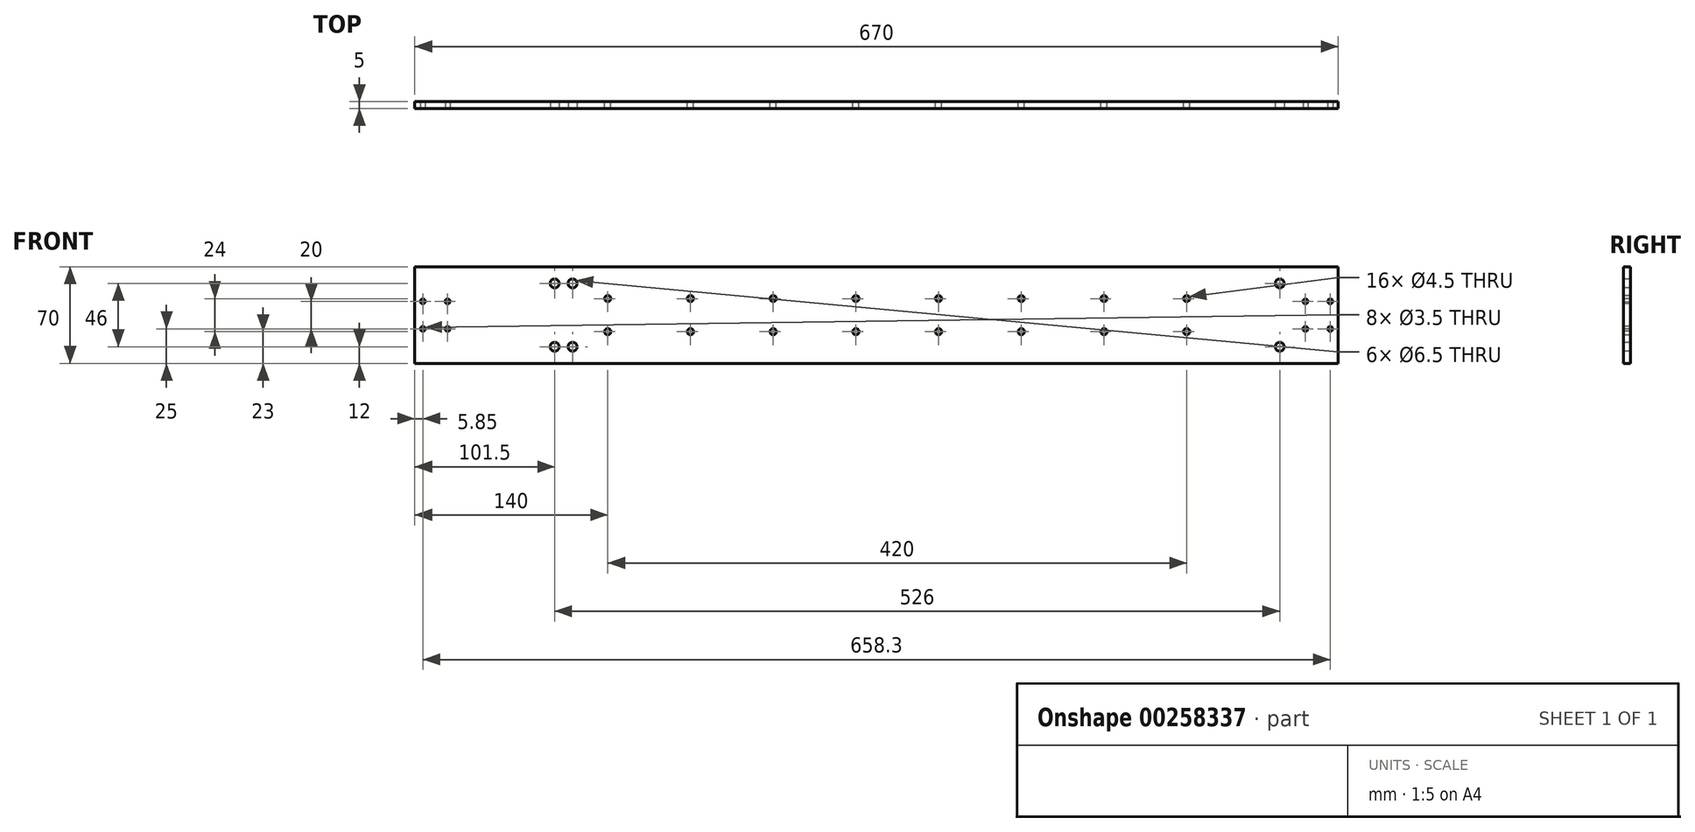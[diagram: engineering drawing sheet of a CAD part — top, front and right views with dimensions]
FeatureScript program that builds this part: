
annotation { "Feature Type Name" : "Feature", "Feature Type Description" : "" }
export const myFeature = defineFeature(function(context is Context, id is Id, definition is map)
    precondition{}
    {
        {
            var Q0;
            Q0=qCreatedBy(makeId("Front.planeOp"),FACE);
            var sketch = newSketch(context, id + "F0", { "sketchPlane" : qUnion([Q0])});
            skLineSegment(sketch, "E0.bottom", {"start": v(335, -35) * mm, "end": v(-335, -35) * mm});
            skLineSegment(sketch, "E0.top", {"start": v(335, 35) * mm, "end": v(-335, 35) * mm});
            skLineSegment(sketch, "E0.left", {"start": v(335, -35) * mm, "end": v(335, 35) * mm});
            skLineSegment(sketch, "E0.right", {"start": v(-335, -35) * mm, "end": v(-335, 35) * mm});
            skPoint(sketch, "E0.middle", {"position": v(0, 0) * mm});
            skSolve(sketch);
        }
        {
            var Q0;
            Q0 = qSketchRegion(id + "F0", true);
            extrude(context, id + "F1", {"entities" : qUnion([Q0]), "depth" : 5 * mm});
        }
        {
            var Q0;
            Q0=makeQuery(id+"F1.opExtrude","CAP_FACE",FACE,{"disambiguationData":[OSD([sQuery(id+"F0.wireOp",EDGE,"E0.bottom"),sQuery(id+"F0.wireOp",EDGE,"E0.top"),sQuery(id+"F0.wireOp",EDGE,"E0.left"),sQuery(id+"F0.wireOp",EDGE,"E0.right")])],"isStart":false});
            var sketch = newSketch(context, id + "F2", { "sketchPlane" : qUnion([Q0])});
            skLineSegment(sketch, "E1", {"start": v(-335, 0) * mm, "end": v(335, 0) * mm, "construction": true});
            skLineSegment(sketch, "E2", {"start": v(0, 35) * mm, "end": v(0, -35) * mm, "construction": true});
            skCircle(sketch, "E3", {"center": v(-329.15, 10) * mm, "radius": 1.75 * mm});
            skCircle(sketch, "E4", {"center": v(-311.15, 10) * mm, "radius": 1.75 * mm});
            skCircle(sketch, "E5", {"center": v(-329.15, -10) * mm, "radius": 1.75 * mm});
            skCircle(sketch, "E6", {"center": v(-311.15, -10) * mm, "radius": 1.75 * mm});
            skCircle(sketch, "E7.MirrorC", {"center": v(329.15, 10) * mm, "radius": 1.75 * mm});
            skCircle(sketch, "E8.MirrorC", {"center": v(311.15, 10) * mm, "radius": 1.75 * mm});
            skCircle(sketch, "E9.MirrorC", {"center": v(311.15, -10) * mm, "radius": 1.75 * mm});
            skCircle(sketch, "E10.MirrorC", {"center": v(329.15, -10) * mm, "radius": 1.75 * mm});
            skSolve(sketch);
        }
        {
            var Q0;
            Q0 = qSketchRegion(id + "F2", true);
            extrude(context, id + "F3", {"entities" : qUnion([Q0]), "operationType" : NewBodyOperationType.REMOVE, "endBound" : BoundingType.UP_TO_NEXT, "oppositeDirection" : true, "depth" : 25 * mm});
        }
        {
            var Q0;
            Q0=makeQuery(id+"F1.opExtrude","CAP_FACE",FACE,{"disambiguationData":[OSD([sQuery(id+"F0.wireOp",EDGE,"E0.bottom"),sQuery(id+"F0.wireOp",EDGE,"E0.top"),sQuery(id+"F0.wireOp",EDGE,"E0.left"),sQuery(id+"F0.wireOp",EDGE,"E0.right")])],"isStart":false});
            var sketch = newSketch(context, id + "F4", { "sketchPlane" : qUnion([Q0])});
            skLineSegment(sketch, "E11", {"start": v(335, 0) * mm, "end": v(-335, 0) * mm, "construction": true});
            skLineSegment(sketch, "E12.bottom", {"start": v(-239, 30) * mm, "end": v(-215, 30) * mm, "construction": true});
            skLineSegment(sketch, "E12.top", {"start": v(-239, -30) * mm, "end": v(-215, -30) * mm, "construction": true});
            skLineSegment(sketch, "E12.left", {"start": v(-239, 30) * mm, "end": v(-239, -30) * mm, "construction": true});
            skLineSegment(sketch, "E12.right", {"start": v(-215, 30) * mm, "end": v(-215, -30) * mm, "construction": true});
            skLineSegment(sketch, "E13.bottom", {"start": v(283, 30) * mm, "end": v(302, 30) * mm, "construction": true});
            skLineSegment(sketch, "E13.top", {"start": v(283, -30) * mm, "end": v(302, -30) * mm, "construction": true});
            skLineSegment(sketch, "E13.left", {"start": v(283, 30) * mm, "end": v(283, -30) * mm, "construction": true});
            skLineSegment(sketch, "E13.right", {"start": v(302, 30) * mm, "end": v(302, -30) * mm, "construction": true});
            skLineSegment(sketch, "E14", {"start": v(302, 0) * mm, "end": v(283, 0) * mm, "construction": true});
            skLineSegment(sketch, "E15", {"start": v(292.5, 30) * mm, "end": v(292.5, -30) * mm, "construction": true});
            skCircle(sketch, "E16", {"center": v(292.5, 23) * mm, "radius": 3.25 * mm});
            skCircle(sketch, "E17", {"center": v(292.5, -23) * mm, "radius": 3.25 * mm});
            skLineSegment(sketch, "E18", {"start": v(-227, 30) * mm, "end": v(-227, -30) * mm, "construction": true});
            skCircle(sketch, "E19", {"center": v(-233.5, 23) * mm, "radius": 3.25 * mm});
            skCircle(sketch, "E20", {"center": v(-220.5, 23) * mm, "radius": 3.25 * mm});
            skCircle(sketch, "E21", {"center": v(-220.5, -23) * mm, "radius": 3.25 * mm});
            skCircle(sketch, "E22", {"center": v(-233.5, -23) * mm, "radius": 3.25 * mm});
            skSolve(sketch);
        }
        {
            var Q0;
            Q0 = qSketchRegion(id + "F4", true);
            extrude(context, id + "F5", {"entities" : qUnion([Q0]), "operationType" : NewBodyOperationType.REMOVE, "endBound" : BoundingType.UP_TO_NEXT, "oppositeDirection" : true, "depth" : 25 * mm});
        }
        {
            var Q0;
            Q0=qCreatedBy(makeId("Front.planeOp"),FACE);
            var sketch = newSketch(context, id + "F6", { "sketchPlane" : qUnion([Q0])});
            skLineSegment(sketch, "E23.bottom", {"start": v(240, 21) * mm, "end": v(-210, 21) * mm, "construction": true});
            skLineSegment(sketch, "E23.top", {"start": v(240, -21) * mm, "end": v(-210, -21) * mm, "construction": true});
            skLineSegment(sketch, "E23.left", {"start": v(240, 21) * mm, "end": v(240, -21) * mm, "construction": true});
            skLineSegment(sketch, "E23.right", {"start": v(-210, 21) * mm, "end": v(-210, -21) * mm, "construction": true});
            skPoint(sketch, "E23.middle", {"position": v(15, 0) * mm});
            skLineSegment(sketch, "E24", {"start": v(240, 0) * mm, "end": v(-210, 0) * mm, "construction": true});
            skLineSegment(sketch, "E25", {"start": v(15, 21) * mm, "end": v(15, -21) * mm, "construction": true});
            skCircle(sketch, "E26", {"center": v(-15, 12) * mm, "radius": 2.25 * mm});
            skCircle(sketch, "E27", {"center": v(-75, 12) * mm, "radius": 2.25 * mm});
            skCircle(sketch, "E28", {"center": v(-135, 12) * mm, "radius": 2.25 * mm});
            skCircle(sketch, "E29", {"center": v(-195, 12) * mm, "radius": 2.25 * mm});
            skLineSegment(sketch, "E30", {"start": v(-15, 12) * mm, "end": v(-75, 12) * mm, "construction": true});
            skLineSegment(sketch, "E31", {"start": v(-75, 12) * mm, "end": v(-135, 12) * mm, "construction": true});
            skLineSegment(sketch, "E32", {"start": v(-135, 12) * mm, "end": v(-195, 12) * mm, "construction": true});
            skCircle(sketch, "E33.MirrorC", {"center": v(225, 12) * mm, "radius": 2.25 * mm});
            skCircle(sketch, "E34.MirrorC", {"center": v(165, 12) * mm, "radius": 2.25 * mm});
            skCircle(sketch, "E35.MirrorC", {"center": v(105, 12) * mm, "radius": 2.25 * mm});
            skCircle(sketch, "E36.MirrorC", {"center": v(45, 12) * mm, "radius": 2.25 * mm});
            skLineSegment(sketch, "E37", {"start": v(45, 12) * mm, "end": v(-15, 12) * mm, "construction": true});
            skCircle(sketch, "E38.MirrorC", {"center": v(-195, -12) * mm, "radius": 2.25 * mm});
            skCircle(sketch, "E39.MirrorC", {"center": v(-135, -12) * mm, "radius": 2.25 * mm});
            skCircle(sketch, "E40.MirrorC", {"center": v(-75, -12) * mm, "radius": 2.25 * mm});
            skCircle(sketch, "E41.MirrorC", {"center": v(-15, -12) * mm, "radius": 2.25 * mm});
            skCircle(sketch, "E42.MirrorC", {"center": v(45, -12) * mm, "radius": 2.25 * mm});
            skCircle(sketch, "E43.MirrorC", {"center": v(105, -12) * mm, "radius": 2.25 * mm});
            skCircle(sketch, "E44.MirrorC", {"center": v(165, -12) * mm, "radius": 2.25 * mm});
            skCircle(sketch, "E45.MirrorC", {"center": v(225, -12) * mm, "radius": 2.25 * mm});
            skLineSegment(sketch, "E46.0", {"start": v(-227, 30) * mm, "end": v(-227, -30) * mm, "construction": true});
            skLineSegment(sketch, "E47.0", {"start": v(292.5, 30) * mm, "end": v(292.5, -30) * mm, "construction": true});
            skLineSegment(sketch, "E48", {"start": v(-227, 0) * mm, "end": v(292.5, 0) * mm, "construction": true});
            skLineSegment(sketch, "E49.0", {"start": v(-215, 30) * mm, "end": v(-215, -30) * mm, "construction": true});
            skSolve(sketch);
        }
        {
            var Q0;
            Q0 = qSketchRegion(id + "F6", true);
            extrude(context, id + "F7", {"entities" : qUnion([Q0]), "operationType" : NewBodyOperationType.REMOVE, "endBound" : BoundingType.UP_TO_NEXT, "depth" : 25 * mm});
        }
    });
